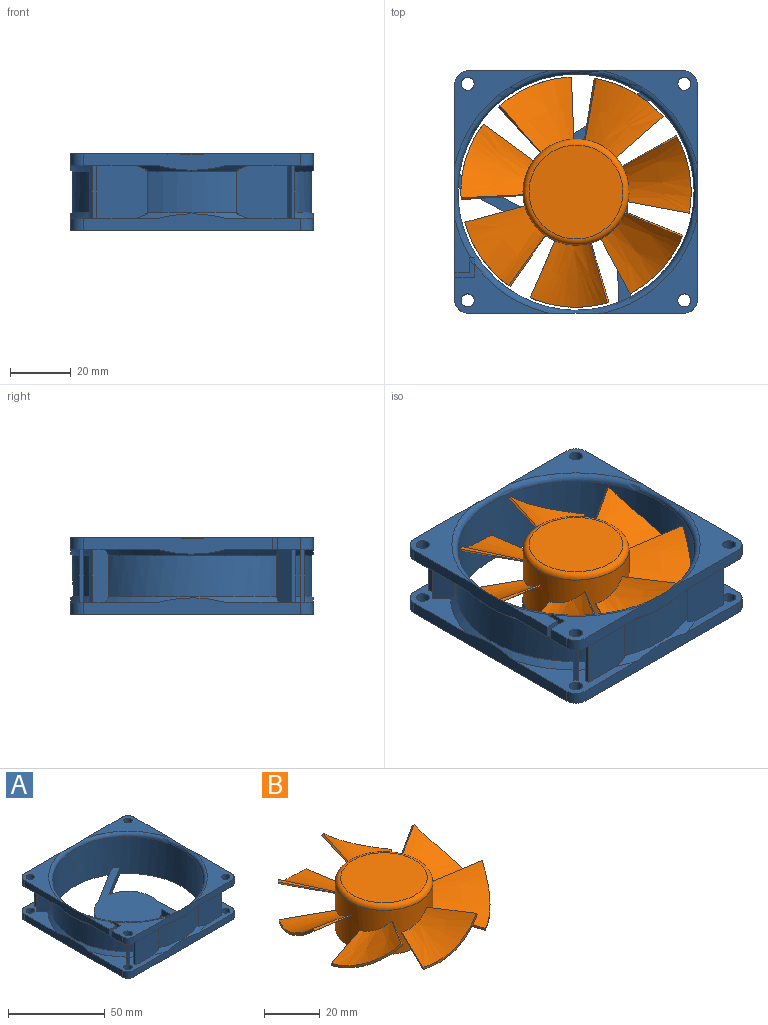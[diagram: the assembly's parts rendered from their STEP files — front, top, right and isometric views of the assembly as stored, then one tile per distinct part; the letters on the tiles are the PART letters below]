
ASSEMBLY  parts=2 mates=1
PART A: 101 faces, bbox 92.7x92.7x26.3 mm
  f0: torus R=41mm, axis (0,0,1), area 739.4mm2, adj f12,f14,f15,f16,f17,f29,f31,f35
  f1: cone r=39.5mm half-angle=45deg, axis (0,0,-1), area 553mm2, adj f13,f20,f21,f22,f26,f30,f34,f38
  f2: cone r=41.5mm half-angle=45deg, axis (0,0,1), area 553mm2, adj f13,f18,f23,f24,f25,f27,f31,f35
  f3: cylinder r=17.5mm len=22.56mm, axis (0,0,-1), area 113.6mm2, adj f28,f64,f65,f68
  f4: cylinder r=2.16mm len=4.32mm, axis (0,0,-1), area 54.3mm2, adj f22,f28
  f5: cylinder r=2.16mm len=4.32mm, axis (0,0,-1), area 54.3mm2, adj f27,f29
  f6: cylinder r=2.16mm len=4.32mm, axis (0,0,-1), area 54.3mm2, adj f21,f28
  f7: cylinder r=2.16mm len=4.32mm, axis (0,0,-1), area 54.3mm2, adj f16,f18
  f8: cylinder r=2.16mm len=4.32mm, axis (0,0,-1), area 54.3mm2, adj f20,f28
  f9: cylinder r=2.16mm len=4.32mm, axis (0,0,-1), area 54.3mm2, adj f15,f24
  f10: cylinder r=2.16mm len=4.32mm, axis (0,0,-1), area 54.3mm2, adj f26,f28
  f11: cylinder r=2.16mm len=4.32mm, axis (0,0,-1), area 54.3mm2, adj f14,f25
  f12: cylinder r=39mm len=78mm, axis (0,0,-1), area 5682.1mm2, adj f0,f28,f62,f63,f64,f65,f66,f67
  f13: cylinder r=39.5mm len=79mm, axis (0,0,1), area 3316.9mm2, adj f1,f2,f87,f88,f89,f90,f91,f92
  f14: plane 31x31mm, normal (0,0,1), area 273.3mm2, adj f0,f11,f39,f41,f43
  f15: plane 31x31mm, normal (0,0,1), area 273.3mm2, adj f0,f9,f31,f43,f45
  f16: plane 31x16.49mm, normal (0,0,1), area 205.4mm2, adj f0,f7,f19,f31,f33,f96,f97
  f17: plane 17.65x5.22mm, normal (0,0,1), area 52.2mm2, adj f0,f35,f98,f99,f100
  f18: plane 28.94x15.63mm, normal (0,0,-1), area 165mm2, adj f2,f7,f19,f31,f33,f54,f55,f57
  f19: plane 7.62x4mm, normal (-1,0,0), area 30.5mm2, adj f16,f18,f33,f96
  f20: plane 28.94x28.94mm, normal (0,0,1), area 225.2mm2, adj f1,f8,f30,f42,f44,f50,f51,f53
  f21: plane 28.94x28.94mm, normal (0,0,1), area 225.2mm2, adj f1,f6,f30,f32,f34,f54,f55,f57
  f22: plane 28.94x28.94mm, normal (0,0,1), area 225.2mm2, adj f1,f4,f34,f36,f38,f58,f59,f61
  f23: plane 15.59x4.93mm, normal (0,0,-1), area 45.8mm2, adj f2,f35,f99,f100
  f24: plane 28.94x28.94mm, normal (0,0,-1), area 225.2mm2, adj f2,f9,f31,f43,f45,f50,f51,f53
  f25: plane 28.94x28.94mm, normal (0,0,-1), area 225.2mm2, adj f2,f11,f39,f41,f43,f46,f47,f49
  f26: plane 28.94x28.94mm, normal (0,0,1), area 225.2mm2, adj f1,f10,f38,f40,f42,f46,f47,f49
  f27: plane 28.94x28.94mm, normal (0,0,-1), area 225.2mm2, adj f2,f5,f35,f37,f39,f58,f59,f61
  f28: plane 80x80mm, normal (0,0,-1), area 2834.4mm2, adj f3,f4,f6,f8,f10,f12,f30,f32
  f29: plane 31x31mm, normal (0,0,1), area 273.3mm2, adj f0,f5,f35,f37,f39
  f30: plane 71.5x5.5mm, normal (0,-1,0), area 308mm2, adj f1,f20,f21,f28,f32,f44
  f31: plane 71.5x5.5mm, normal (0,-1,0), area 305.5mm2, adj f0,f2,f15,f16,f18,f24,f33,f45
  f32: cylinder r=4.25mm len=4.25mm, axis (0,0,-1), area 26.7mm2, adj f21,f28,f30,f34
  f33: cylinder r=4.25mm len=4.25mm, axis (0,0,-1), area 26.7mm2, adj f16,f18,f19,f31
  f34: plane 71.5x5.5mm, normal (-1,0,0), area 308mm2, adj f1,f21,f22,f28,f32,f36
  f35: plane 63.25x6.36mm, normal (-1,0,0), area 269.1mm2, adj f0,f2,f17,f23,f27,f29,f37,f100
  f36: cylinder r=4.25mm len=4.25mm, axis (0,0,-1), area 26.7mm2, adj f22,f28,f34,f38
  f37: cylinder r=4.25mm len=4.25mm, axis (0,0,-1), area 26.7mm2, adj f27,f29,f35,f39
  f38: plane 71.5x5.5mm, normal (0,1,0), area 308mm2, adj f1,f22,f26,f28,f36,f40
  f39: plane 71.5x5.5mm, normal (0,1,0), area 305.5mm2, adj f0,f2,f14,f25,f27,f29,f37,f41
  f40: cylinder r=4.25mm len=4.25mm, axis (0,0,-1), area 26.7mm2, adj f26,f28,f38,f42
  f41: cylinder r=4.25mm len=4.25mm, axis (0,0,-1), area 26.7mm2, adj f14,f25,f39,f43
  f42: plane 71.5x5.5mm, normal (1,0,0), area 308mm2, adj f1,f20,f26,f28,f40,f44
  f43: plane 72.35x6.36mm, normal (1,0,0), area 305.5mm2, adj f0,f2,f14,f15,f24,f25,f41,f45
  f44: cylinder r=4.25mm len=4.25mm, axis (0,0,-1), area 26.7mm2, adj f20,f28,f30,f42
  f45: cylinder r=4.25mm len=4.25mm, axis (0,0,-1), area 26.7mm2, adj f15,f24,f31,f43
  f46: plane 17.4x1.04mm, normal (0.71,0.71,0), area 25.7mm2, adj f25,f26,f47,f49
  f47: plane 17.4x5.18mm, normal (-0.71,0.71,0), area 125.2mm2, adj f1,f2,f25,f26,f46,f48
  f48: cylinder r=40mm len=14.4mm, axis (0,0,-1), area 21.3mm2, adj f1,f2,f47,f49
  f49: plane 17.4x5.18mm, normal (0.71,-0.71,0), area 125.2mm2, adj f1,f2,f25,f26,f46,f48
  f50: plane 17.4x1.04mm, normal (0.71,-0.71,0), area 25.7mm2, adj f20,f24,f51,f53
  f51: plane 17.4x5.18mm, normal (0.71,0.71,0), area 125.2mm2, adj f1,f2,f20,f24,f50,f52
  f52: cylinder r=40mm len=14.4mm, axis (0,0,-1), area 21.3mm2, adj f1,f2,f51,f53
  f53: plane 17.4x5.18mm, normal (-0.71,-0.71,0), area 125.2mm2, adj f1,f2,f20,f24,f50,f52
  f54: plane 17.4x1.04mm, normal (-0.71,-0.71,0), area 25.7mm2, adj f18,f21,f55,f57
  f55: plane 17.4x5.18mm, normal (0.71,-0.71,0), area 125.2mm2, adj f1,f2,f18,f21,f54,f56
  f56: cylinder r=40mm len=14.4mm, axis (0,0,-1), area 21.3mm2, adj f1,f2,f55,f57
  f57: plane 17.4x5.18mm, normal (-0.71,0.71,0), area 125.2mm2, adj f1,f2,f18,f21,f54,f56
  f58: plane 17.4x1.04mm, normal (-0.71,0.71,0), area 25.7mm2, adj f22,f27,f59,f61
  f59: plane 17.4x5.18mm, normal (-0.71,-0.71,0), area 125.2mm2, adj f1,f2,f22,f27,f58,f60
  f60: cylinder r=40mm len=14.4mm, axis (0,0,-1), area 21.3mm2, adj f1,f2,f59,f61
  f61: plane 17.4x5.18mm, normal (0.71,0.71,0), area 125.2mm2, adj f1,f2,f22,f27,f58,f60
  f62: plane 24.92x4mm, normal (-1,-0.03,0), area 99.7mm2, adj f12,f28,f64,f85
  f63: plane 30.4x4mm, normal (1,0.03,0), area 121.7mm2, adj f12,f28,f64,f86
  f64: plane 69.28x63.39mm, normal (0,0,1), area 1286.8mm2, adj f3,f12,f62,f63,f65,f66,f67,f68
  f65: plane 22.02x11.71mm, normal (0.47,0.88,0), area 99.7mm2, adj f3,f12,f28,f64
  f66: plane 26.86x14.28mm, normal (-0.47,-0.88,0), area 121.7mm2, adj f12,f28,f64,f85
  f67: plane 21.15x13.21mm, normal (0.53,-0.85,0), area 99.7mm2, adj f12,f28,f64,f86
  f68: plane 25.8x16.12mm, normal (-0.53,0.85,0), area 121.7mm2, adj f3,f12,f28,f64
  f69: cylinder r=40mm len=14.4mm, axis (0,0,-1), area 52.2mm2, adj f1,f2,f70,f72
  f70: plane 17.49x13.58mm, normal (0,-1,0), area 229.9mm2, adj f1,f2,f25,f26,f69,f71
  f71: plane 17.4x1.48mm, normal (1,0,0), area 25.7mm2, adj f25,f26,f70,f72
  f72: plane 17.52x16.92mm, normal (0,1,0), area 286.6mm2, adj f1,f2,f25,f26,f69,f71
  f73: plane 17.4x1.48mm, normal (-1,0,0), area 25.7mm2, adj f22,f27,f74,f76
  f74: plane 17.49x13.58mm, normal (0,-1,0), area 229.9mm2, adj f1,f2,f22,f27,f73,f75
  f75: cylinder r=40mm len=14.4mm, axis (0,0,-1), area 52.2mm2, adj f1,f2,f74,f76
  f76: plane 17.52x16.92mm, normal (0,1,0), area 286.6mm2, adj f1,f2,f22,f27,f73,f75
  f77: plane 17.52x16.92mm, normal (0,-1,0), area 286.6mm2, adj f1,f2,f18,f21,f78,f80
  f78: cylinder r=40mm len=14.4mm, axis (0,0,-1), area 52.2mm2, adj f1,f2,f77,f79
  f79: plane 17.49x13.58mm, normal (0,1,0), area 229.9mm2, adj f1,f2,f18,f21,f78,f80
  f80: plane 17.4x1.48mm, normal (-1,0,0), area 25.7mm2, adj f18,f21,f77,f79
  f81: cylinder r=40mm len=14.4mm, axis (0,0,-1), area 52.2mm2, adj f1,f2,f82,f84
  f82: plane 17.52x16.92mm, normal (0,-1,0), area 286.6mm2, adj f1,f2,f20,f24,f81,f83
  f83: plane 17.4x1.48mm, normal (1,0,0), area 25.7mm2, adj f20,f24,f82,f84
  f84: plane 17.49x13.58mm, normal (0,1,0), area 229.9mm2, adj f1,f2,f20,f24,f81,f83
  f85: cylinder r=17.5mm len=25.36mm, axis (0,0,-1), area 113.6mm2, adj f28,f62,f64,f66
  f86: cylinder r=17.5mm len=21.36mm, axis (0,0,-1), area 113.6mm2, adj f28,f63,f64,f67
  f87: plane 0.87x0.24mm, normal (0,0,-1), area 0.2mm2, adj f13,f88,f93,f94
  f88: plane 2.5x0.24mm, normal (1,0,0), area 0.6mm2, adj f13,f87,f89,f94
  f89: plane 1.76x0.25mm, normal (0,0,-1), area 0.4mm2, adj f13,f88,f90,f94
  f90: plane 2.5x0.24mm, normal (-1,0,0), area 0.6mm2, adj f13,f89,f91,f94
  f91: plane 0.87x0.24mm, normal (0,0,-1), area 0.2mm2, adj f13,f90,f92,f94
  f92: plane 2.5x1.75mm, normal (-0.82,0,0.57), area 0.7mm2, adj f13,f91,f93,f94
  f93: plane 2.5x1.75mm, normal (0.82,0,0.57), area 0.7mm2, adj f13,f87,f92,f94
  f94: plane 5x3.5mm, normal (0,1,0), area 8.8mm2, adj f87,f88,f89,f90,f91,f92,f93
  f95: plane 2.65x1.48mm, normal (0,0,1), area 2.3mm2, adj f2,f97,f98,f99
  f96: plane 6.41x4mm, normal (0,1,0), area 25.6mm2, adj f16,f18,f19,f97
  f97: plane 6.42x4.01mm, normal (-1,0,0), area 25.5mm2, adj f0,f16,f18,f95,f96,f98
  f98: plane 4.01x1.49mm, normal (0,-1,0), area 5.8mm2, adj f0,f17,f95,f97,f99
  f99: plane 4.93x4mm, normal (1,0,0), area 19.7mm2, adj f17,f23,f95,f98,f100
  f100: plane 4.93x4mm, normal (0,-1,0), area 19.7mm2, adj f17,f23,f35,f99
PART B: 39 faces, bbox 79.1x78.3x21.4 mm
  f0: cylinder r=38mm len=25.68mm, axis (0,0,-1), area 28.8mm2, adj f22,f23,f24,f25
  f1: torus R=15.5mm, axis (0,0,-1), area 331.1mm2, adj f2,f31
  f2: cylinder r=17.5mm len=35mm, axis (0,0,1), area 2090.2mm2, adj f1,f3,f5,f6,f7,f8,f9,f10
  f3: plane 35x35mm, normal (0,0,-1), area 962.1mm2, adj f2
  f4: cylinder r=38mm len=21.28mm, axis (0,0,-1), area 28.9mm2, adj f5,f6,f7,f8
  f5: bspline ~27.32x26.27mm, area 404.3mm2, adj f2,f4,f6,f8
  f6: plane 17x12.22mm, normal (0.68,-0.32,0.66), area 14.5mm2, adj f2,f4,f5,f7
  f7: bspline ~39.25x33.01mm, area 412mm2, adj f2,f4,f6,f8
  f8: plane 19.8x5.43mm, normal (-0.25,0.96,-0.08), area 14mm2, adj f2,f4,f5,f7
  f9: bspline ~39.98x26.26mm, area 404.3mm2, adj f2,f10,f12,f36
  f10: plane 20.49x4.78mm, normal (0.18,-0.73,0.66), area 14.5mm2, adj f2,f9,f11,f36
  f11: bspline ~40.11x26.66mm, area 412mm2, adj f2,f10,f12,f36
  f12: plane 16.57x12.16mm, normal (0.6,0.8,-0.08), area 14mm2, adj f2,f9,f11,f36
  f13: cylinder r=38mm len=24.08mm, axis (0,0,-1), area 28.9mm2, adj f14,f15,f16,f17
  f14: bspline ~25.79x24.43mm, area 404.3mm2, adj f2,f13,f15,f17
  f15: plane 15.58x14.03mm, normal (-0.46,-0.6,0.66), area 14.5mm2, adj f2,f13,f14,f16
  f16: bspline ~25.65x24.87mm, area 412mm2, adj f2,f13,f15,f17
  f17: plane 20.49x2.91mm, normal (1,0.03,-0.08), area 14mm2, adj f2,f13,f14,f16
  f18: bspline ~39.46x30.79mm, area 404.3mm2, adj f2,f19,f21,f37
  f19: plane 20.29x4.78mm, normal (-0.75,-0.01,0.66), area 14.5mm2, adj f2,f18,f20,f37
  f20: bspline ~39.69x30.72mm, area 412mm2, adj f2,f19,f21,f37
  f21: plane 15.53x13.47mm, normal (0.65,-0.76,-0.08), area 14mm2, adj f2,f18,f20,f37
  f22: bspline ~25.9x23.93mm, area 425.4mm2, adj f0,f2,f23,f25
  f23: plane 18.15x10.35mm, normal (-0.48,0.58,0.66), area 14.5mm2, adj f0,f2,f22,f24
  f24: bspline ~26.49x23.95mm, area 433.8mm2, adj f0,f2,f23,f25
  f25: plane 20.17x3.8mm, normal (-0.19,-0.98,-0.08), area 14mm2, adj f0,f2,f22,f24
  f26: cylinder r=38mm len=19.36mm, axis (0,0,-1), area 28.9mm2, adj f27,f28,f29,f30
  f27: bspline ~27.49x26.79mm, area 404.3mm2, adj f2,f26,f28,f30
  f28: plane 19.13x8.25mm, normal (0.16,0.74,0.66), area 14.5mm2, adj f2,f26,f27,f29
  f29: bspline ~37.29x35.88mm, area 412mm2, adj f2,f26,f28,f30
  f30: plane 18.12x9.69mm, normal (-0.88,-0.46,-0.08), area 14mm2, adj f2,f26,f27,f29
  f31: plane 31x31mm, normal (0,0,1), area 754.8mm2, adj f1
  f32: plane 18.84x8.18mm, normal (-0.91,0.4,-0.08), area 14mm2, adj f2,f33,f35,f38
  f33: bspline ~38.49x27.2mm, area 397.4mm2, adj f2,f32,f34,f38
  f34: plane 19.82x6.15mm, normal (0.67,0.34,0.66), area 14.5mm2, adj f2,f33,f35,f38
  f35: bspline ~38.51x27.61mm, area 404.6mm2, adj f2,f32,f34,f38
  f36: bspline ~26.93x15.6mm, area 28.9mm2, adj f9,f10,f11,f12
  f37: bspline ~24.57x15.6mm, area 28.9mm2, adj f18,f19,f20,f21
  f38: bspline ~27.94x15.6mm, area 28.9mm2, adj f32,f33,f34,f35
PLACE A at identity
PLACE B at identity
MATE revolute B.f0 <-> A.f0  axis (0,0,-1) through (0,0,4)mm
